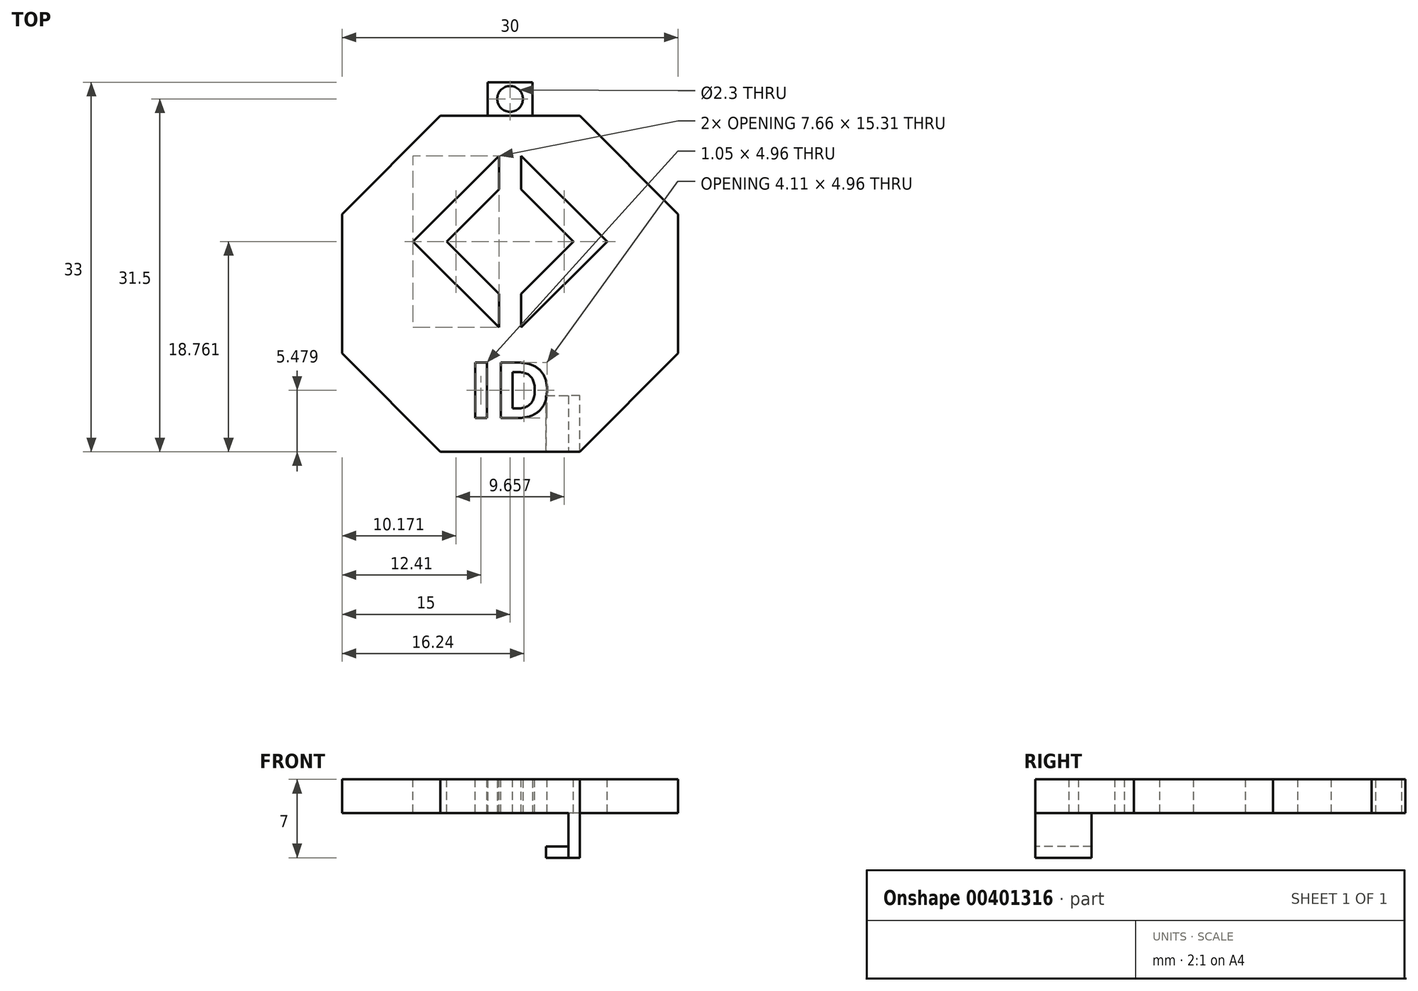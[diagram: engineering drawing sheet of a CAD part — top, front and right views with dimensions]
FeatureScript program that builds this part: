
annotation { "Feature Type Name" : "Feature", "Feature Type Description" : "" }
export const myFeature = defineFeature(function(context is Context, id is Id, definition is map)
    precondition{}
    {
        {
            var Q0;
            Q0=qCreatedBy(makeId("Top.planeOp"),FACE);
            var sketch = newSketch(context, id + "F0", { "sketchPlane" : qUnion([Q0])});
            skCircle(sketch, "E0.cCircle", {"center": v(0, 0) * mm, "radius": 15 * mm, "construction": true});
            skLineSegment(sketch, "E0.0", {"start": v(15, 6.21) * mm, "end": v(15, -6.21) * mm});
            skLineSegment(sketch, "E0.1", {"start": v(15, -6.21) * mm, "end": v(6.21, -15) * mm});
            skLineSegment(sketch, "E0.2", {"start": v(6.21, -15) * mm, "end": v(-6.21, -15) * mm});
            skLineSegment(sketch, "E0.3", {"start": v(-6.21, -15) * mm, "end": v(-15, -6.21) * mm});
            skLineSegment(sketch, "E0.4", {"start": v(-15, -6.21) * mm, "end": v(-15, 6.21) * mm});
            skLineSegment(sketch, "E0.5", {"start": v(-15, 6.21) * mm, "end": v(-6.21, 15) * mm});
            skLineSegment(sketch, "E0.6", {"start": v(-6.21, 15) * mm, "end": v(6.21, 15) * mm});
            skLineSegment(sketch, "E0.7", {"start": v(6.21, 15) * mm, "end": v(15, 6.21) * mm});
            skPoint(sketch, "E0.0.midPoint", {"position": v(15, 0) * mm});
            skLineSegment(sketch, "E1", {"start": v(0, 0) * mm, "end": v(-15, 0) * mm, "construction": true});
            skSolve(sketch);
        }
        {
            var Q0;
            Q0=qSketchRegion(id+"F0",true);
            extrude(context, id + "F1", {"entities" : qUnion([Q0]), "depth" : 3 * mm});
        }
        {
            var Q0;
            Q0=makeQuery(id+"F1.opExtrude","CAP_FACE",FACE,{"disambiguationData":[OSD([sQuery(id+"F0.wireOp",EDGE,"E0.0"),sQuery(id+"F0.wireOp",EDGE,"E0.1"),sQuery(id+"F0.wireOp",EDGE,"E0.2"),sQuery(id+"F0.wireOp",EDGE,"E0.3"),sQuery(id+"F0.wireOp",EDGE,"E0.4"),sQuery(id+"F0.wireOp",EDGE,"E0.5"),sQuery(id+"F0.wireOp",EDGE,"E0.6"),sQuery(id+"F0.wireOp",EDGE,"E0.7")])],"isStart":false});
            var sketch = newSketch(context, id + "F2", { "sketchPlane" : qUnion([Q0])});
            skText(sketch, "E2", { "text": "ID", "fontName": "OpenSans-Bold.ttf"});
            skArc(sketch, "E3.cCircle", {"start": v(2.83, 0.93) * mm, "mid": v(0, 7.76) * mm, "end": v(-2.83, 0.93) * mm, "construction": true});
            skLineSegment(sketch, "E3.0", {"start": v(5.66, 3.76) * mm, "end": v(1, -0.9) * mm});
            skLineSegment(sketch, "E3.2", {"start": v(-5.66, 3.76) * mm, "end": v(-1, 8.42) * mm});
            skLineSegment(sketch, "E3.3", {"start": v(1, 8.42) * mm, "end": v(5.66, 3.76) * mm});
            skPoint(sketch, "E3.0.midPoint", {"position": v(2.83, 0.93) * mm});
            skLineSegment(sketch, "E4", {"start": v(-5.66, 3.76) * mm, "end": v(0, 3.76) * mm, "construction": true});
            skLineSegment(sketch, "E5.1", {"start": v(8.66, 3.76) * mm, "end": v(1, -3.9) * mm});
            skLineSegment(sketch, "E5.3", {"start": v(-8.66, 3.76) * mm, "end": v(-1, 11.42) * mm});
            skPoint(sketch, "E5.0.midPoint", {"position": v(4.33, 8.1) * mm});
            skLineSegment(sketch, "E6", {"start": v(-8.66, 3.76) * mm, "end": v(-5.66, 3.76) * mm, "construction": true});
            skPoint(sketch, "E7.orphan", {"position": v(0, -1.9) * mm});
            skPoint(sketch, "E8.orphan", {"position": v(0, -4.9) * mm});
            skPoint(sketch, "E9.orphan", {"position": v(0.45, -660.17) * mm});
            skPoint(sketch, "E10.orphan", {"position": v(-0.45, -23.95) * mm});
            skLineSegment(sketch, "E11.trimOffspring", {"start": v(0, 3.76) * mm, "end": v(8.66, 3.76) * mm, "construction": true});
            skPoint(sketch, "E12.orphan", {"position": v(0, 9.42) * mm});
            skPoint(sketch, "E13.orphan", {"position": v(0, 12.42) * mm});
            skPoint(sketch, "E14.bottom.end.orphan", {"position": v(0.45, 31.48) * mm});
            skPoint(sketch, "E14.bottom.start.orphan", {"position": v(-0.45, 667.69) * mm});
            skPoint(sketch, "E15.firstSnap0", {"position": v(-10.6, -10.6) * mm});
            skPoint(sketch, "E15.secondSnap0", {"position": v(10.6, 10.6) * mm});
            skPoint(sketch, "E16.startSnap0", {"position": v(0.45, 11.37) * mm});
            skLineSegment(sketch, "E17", {"start": v(1, 11.42) * mm, "end": v(1, 8.42) * mm});
            skLineSegment(sketch, "E18", {"start": v(-1, 11.42) * mm, "end": v(-1, 8.42) * mm});
            skPoint(sketch, "E19.orphan", {"position": v(0.45, 12.87) * mm});
            skLineSegment(sketch, "E20.trimOffspring", {"start": v(1, 11.42) * mm, "end": v(8.66, 3.76) * mm});
            skPoint(sketch, "E21.trimOffspring.end.orphan", {"position": v(0.45, 9.87) * mm});
            skLineSegment(sketch, "E22.trimOffspring", {"start": v(-1, -0.9) * mm, "end": v(-5.66, 3.76) * mm});
            skLineSegment(sketch, "E23.trimOffspring", {"start": v(-1, -0.9) * mm, "end": v(-1, -3.9) * mm});
            skLineSegment(sketch, "E24.trimOffspring", {"start": v(1, -0.9) * mm, "end": v(1, -3.9) * mm});
            skLineSegment(sketch, "E25.trimOffspring", {"start": v(-1, -3.9) * mm, "end": v(-8.66, 3.76) * mm});
            const initialGuessF2  = {"E2": [-0.00374, -0.012, 1, 0, 0.005]};
            skSetInitialGuess(sketch, initialGuessF2);
            skSolve(sketch);
        }
        {
            var Q0;
            Q0=qSketchRegion(id+"F2",true);
            extrude(context, id + "F3", {"entities" : qUnion([Q0]), "operationType" : NewBodyOperationType.REMOVE, "endBound" : BoundingType.THROUGH_ALL, "oppositeDirection" : true, "depth" : 3 * mm});
        }
        {
            var Q0;
            Q0=makeQuery(id+"F1.opExtrude","CAP_FACE",FACE,{"disambiguationData":[OSD([sQuery(id+"F0.wireOp",EDGE,"E0.0"),sQuery(id+"F0.wireOp",EDGE,"E0.1"),sQuery(id+"F0.wireOp",EDGE,"E0.2"),sQuery(id+"F0.wireOp",EDGE,"E0.3"),sQuery(id+"F0.wireOp",EDGE,"E0.4"),sQuery(id+"F0.wireOp",EDGE,"E0.5"),sQuery(id+"F0.wireOp",EDGE,"E0.6"),sQuery(id+"F0.wireOp",EDGE,"E0.7")])],"isStart":true});
            var sketch = newSketch(context, id + "F4", { "sketchPlane" : qUnion([Q0])});
            skLineSegment(sketch, "E26.bottom", {"start": v(6.21, 15) * mm, "end": v(5.21, 15) * mm});
            skLineSegment(sketch, "E26.top", {"start": v(6.21, 10) * mm, "end": v(5.21, 10) * mm});
            skLineSegment(sketch, "E26.left", {"start": v(6.21, 15) * mm, "end": v(6.21, 10) * mm});
            skLineSegment(sketch, "E26.right", {"start": v(5.21, 15) * mm, "end": v(5.21, 10) * mm});
            skSolve(sketch);
        }
        {
            var Q0;
            Q0=qSketchRegion(id+"F4",true);
            extrude(context, id + "F5", {"entities" : qUnion([Q0]), "operationType" : NewBodyOperationType.ADD, "depth" : 4 * mm});
        }
        {
            var Q0;
            Q0=makeQuery(id+"F5.opExtrude","SWEPT_FACE",FACE,{"disambiguationData":[OSD([sQuery(id+"F4.wireOp",EDGE,"E26.right")])]});
            var sketch = newSketch(context, id + "F6", { "sketchPlane" : qUnion([Q0])});
            skLineSegment(sketch, "E27.bottom", {"start": v(10, -4) * mm, "end": v(15, -4) * mm});
            skLineSegment(sketch, "E27.top", {"start": v(10, -3) * mm, "end": v(15, -3) * mm});
            skLineSegment(sketch, "E27.left", {"start": v(10, -4) * mm, "end": v(10, -3) * mm});
            skLineSegment(sketch, "E27.right", {"start": v(15, -4) * mm, "end": v(15, -3) * mm});
            skSolve(sketch);
        }
        {
            var Q0;
            Q0=makeQuery(id+"F6.imprint","IMPRINT",FACE,{"disambiguationData":[TD([[makeQuery(id+"F6.imprint","IMPRINT",EDGE,{"derivedFrom":sQuery(id+"F6.wireOp",EDGE,"E27.bottom")}),-1.0]])]});
            var Q1;
            Q1=sQuery(id+"F6.wireOp",EDGE,"E27.top");
            var Q2;
            Q2=sQuery(id+"F6.wireOp",EDGE,"E27.bottom");
            var Q3;
            Q3=sQuery(id+"F6.wireOp",EDGE,"E27.right");
            var Q4;
            Q4=sQuery(id+"F6.wireOp",EDGE,"E27.left");
            extrude(context, id + "F7", {"entities" : qUnion([Q0]), "surfaceEntities" : qUnion([Q1, Q2, Q3, Q4]), "depth" : 2 * mm});
        }
        {
            var Q0;
            Q0=makeQuery(id+"F1.opExtrude","SWEPT_FACE",FACE,{"disambiguationData":[OSD([sQuery(id+"F0.wireOp",EDGE,"E0.6")])]});
            var sketch = newSketch(context, id + "F8", { "sketchPlane" : qUnion([Q0])});
            skLineSegment(sketch, "E28.bottom", {"start": v(2, 3) * mm, "end": v(-2, 3) * mm});
            skLineSegment(sketch, "E28.top", {"start": v(2, 0) * mm, "end": v(-2, 0) * mm});
            skLineSegment(sketch, "E28.left", {"start": v(2, 3) * mm, "end": v(2, 0) * mm});
            skLineSegment(sketch, "E28.right", {"start": v(-2, 3) * mm, "end": v(-2, 0) * mm});
            skPoint(sketch, "E28.middle", {"position": v(0, 1.5) * mm});
            skPoint(sketch, "E28.middle.positionSnap0", {"position": v(0, 3) * mm});
            skPoint(sketch, "E28.centerSnap0", {"position": v(0, 3) * mm});
            skSolve(sketch);
        }
        {
            var Q0;
            Q0=qSketchRegion(id+"F8",true);
            extrude(context, id + "F9", {"entities" : qUnion([Q0]), "depth" : 3 * mm});
        }
        {
            var Q0;
            Q0=makeQuery(id+"F9.opExtrude","SWEPT_FACE",FACE,{"disambiguationData":[OSD([sQuery(id+"F8.wireOp",EDGE,"E28.top")])]});
            var sketch = newSketch(context, id + "F10", { "sketchPlane" : qUnion([Q0])});
            skCircle(sketch, "E29", {"center": v(0, -16.5) * mm, "radius": 1.15 * mm});
            skLineSegment(sketch, "E30", {"start": v(0, -16.5) * mm, "end": v(0, -15) * mm, "construction": true});
            skLineSegment(sketch, "E31", {"start": v(0, -16.5) * mm, "end": v(0, -18) * mm, "construction": true});
            skSolve(sketch);
        }
        {
            var Q0;
            Q0=qSketchRegion(id+"F10",true);
            extrude(context, id + "F11", {"entities" : qUnion([Q0]), "operationType" : NewBodyOperationType.REMOVE, "endBound" : BoundingType.THROUGH_ALL, "oppositeDirection" : true, "depth" : 25 * mm});
        }
    });
